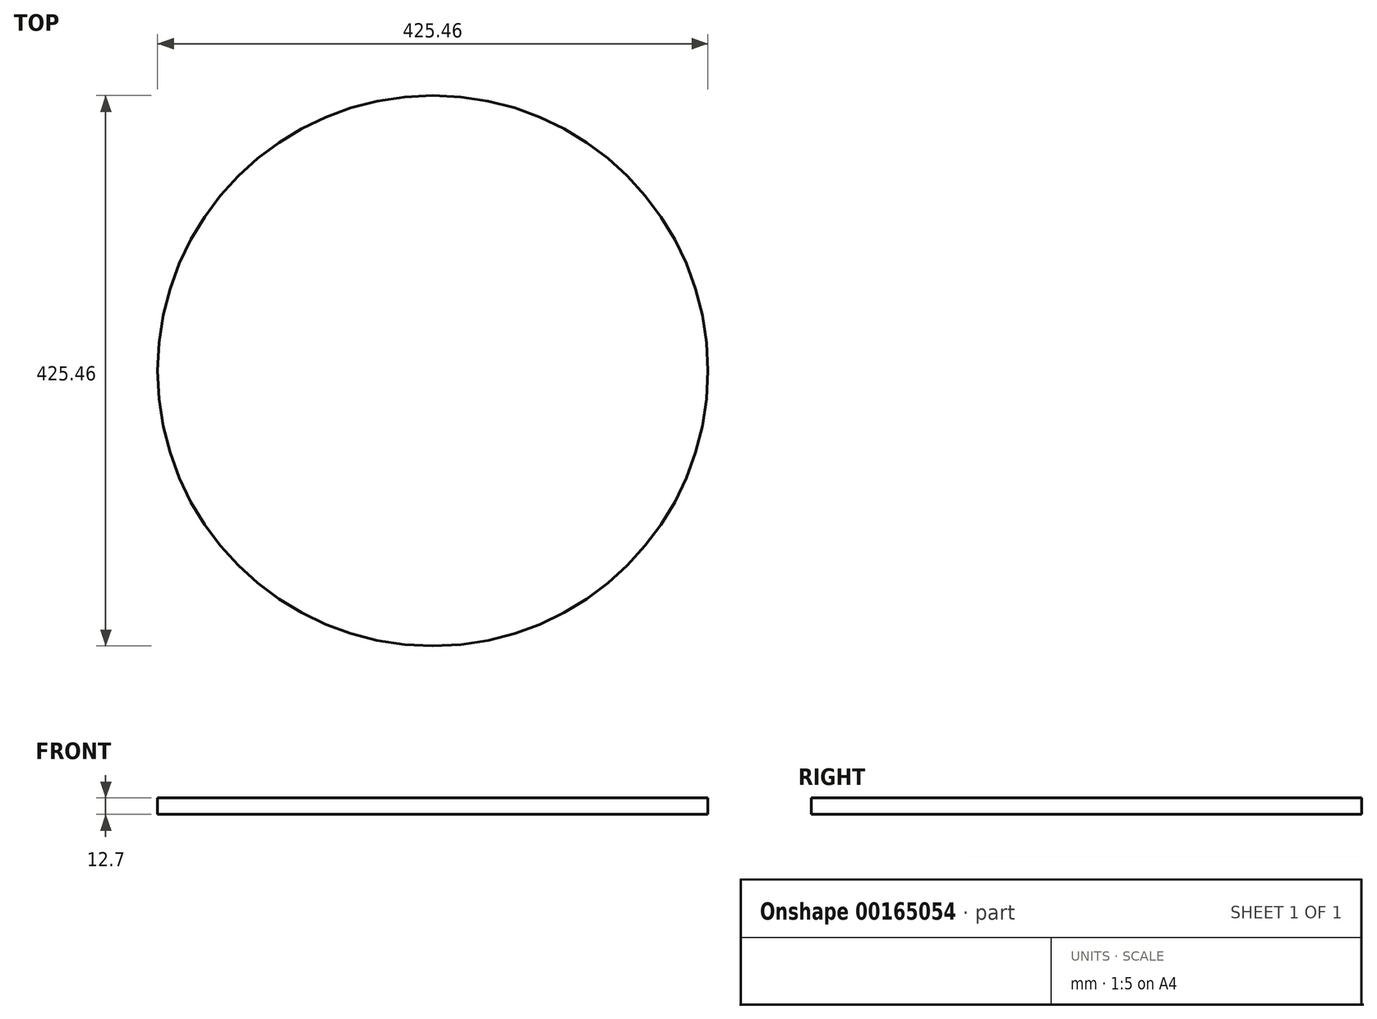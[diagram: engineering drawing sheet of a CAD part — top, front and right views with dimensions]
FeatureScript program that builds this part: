
annotation { "Feature Type Name" : "Feature", "Feature Type Description" : "" }
export const myFeature = defineFeature(function(context is Context, id is Id, definition is map)
    precondition{}
    {
        {
            var Q0;
            Q0=qCreatedBy(makeId("Top.planeOp"),FACE);
            var sketch = newSketch(context, id + "F0", { "sketchPlane" : qUnion([Q0])});
            skCircle(sketch, "E0", {"center": v(0, 0) * mm, "radius": 212.72 * mm});
            skSolve(sketch);
        }
        {
            var Q0;
            Q0=qSketchRegion(id+"F0",true);
            extrude(context, id + "F1", {"entities" : qUnion([Q0]), "depth" : 12.7 * mm});
        }
    });
